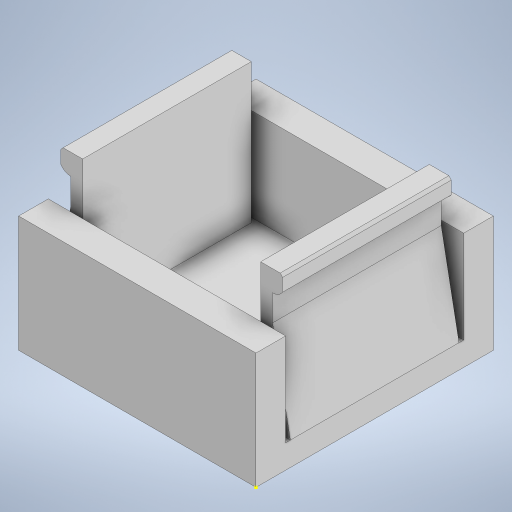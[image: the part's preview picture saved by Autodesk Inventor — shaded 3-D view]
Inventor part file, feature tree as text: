
AUTODESK INVENTOR PART (.ipt)
format: ipt  version: 2023 (Build 270158000, 158)  size: 304,640 bytes
history: native  units: in
note: dims shown in document units (in); Inventor stores cm internally (conversion verified against a paired STEP export)
features: sketch x7, extrude x6
ambient origin geometry x8: Origin, YZ Plane, XZ Plane, XY Plane, X Axis, Y Axis, Z Axis, Center Point
bodies: Solid1 (feature_tree)
feature tree (13):
  sketch  "Sketch1"  dims[d0=1.0in d1=1.0in]
  extrude  "Extrusion1"  Depth=1.0in
  extrude  "Extrusion2"  Depth=0.125in
  extrude  "Extrusion3"  Depth=0.125in
  extrude  "Extrusion4"  Depth=0.125in TaperAngle=0.0deg
  extrude  "Extrusion6"  Depth=0.1in
  extrude  "Extrusion7"  Depth=0.05in
  sketch  "Sketch2"  dims[d2=0.7in d3=0.0in d4=0.125in]
  sketch  "Sketch3"  dims[d5=0.125in d6=0.125in]
  sketch  "Sketch4"  dims[d7=0.125in d8=0.6in d9=0.0in]
  sketch  "Sketch5"  dims[d10=0.1in d11=0.1in]
  sketch  "Sketch7"  dims[d12=0.05in d13=0.05in]
  sketch  "Sketch8"  dims[d14=0.05in d15=0.05in d16=0.05in d17=0.21in d18=0.05in d19=0.21in d20=1.0in d21=0.0in d22=1.0in d23=0.0in d25=0.1447in d26=0.1447in d32=0.7283in d33=0.0in d34=0.0079in d35=0.0394in d36=0.0079in d37=0.0118in d38=0.0in d39=0.7283in d40=0.0in]
